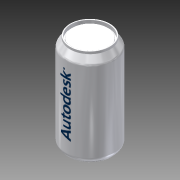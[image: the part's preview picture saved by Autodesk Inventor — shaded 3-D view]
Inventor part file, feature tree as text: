
AUTODESK INVENTOR PART (.ipt)
format: ipt  version: 2013 (Build 170138000, 138)  size: 232,960 bytes
history: native  units: in
note: dims shown in document units (in); Inventor stores cm internally (conversion verified against a paired STEP export)
features: other x4, sketch x4, revolve x3, plane x2, fillet x2, projected_geometry x1
ambient origin geometry x8: Origin, YZ Plane, XZ Plane, XY Plane, X Axis, Y Axis, Z Axis, Center Point
bodies: Solid1 (feature_tree)
feature tree (16):
  revolve  "Revolution1"  [1 undecoded]
  plane  "Work Plane1"
  revolve  "Revolution2"  Angle=90.0deg
  revolve  "Revolution3"  Angle=90.0deg
  fillet  "Fillet1"  [1 undecoded]
  fillet  "Fillet2"  Radius=0.25in
  plane  "Work Plane2"
  other  "Decal1"
  other  "Work Axis2"
  sketch  "Sketch1"  dims[d0=2.5in d2=4.25in]
  other  "Work Axis1"
  sketch  "Sketch2"  dims[d3=90.0deg d4=90.0deg]
  sketch  "Sketch3"  dims[d5=0.125in d6=90.0deg d7=90.0deg d8=0.25in]
  projected_geometry  "Projected Loop1"
  sketch  "Sketch4"  dims[d9=0.02in d10=1.5625in]
  other  "Image1"
note: 2 required parameter values undecoded (feature->parameter linkage not recoverable at this tier; creation-order binding heuristic only, values carry confidence <= 0.55)